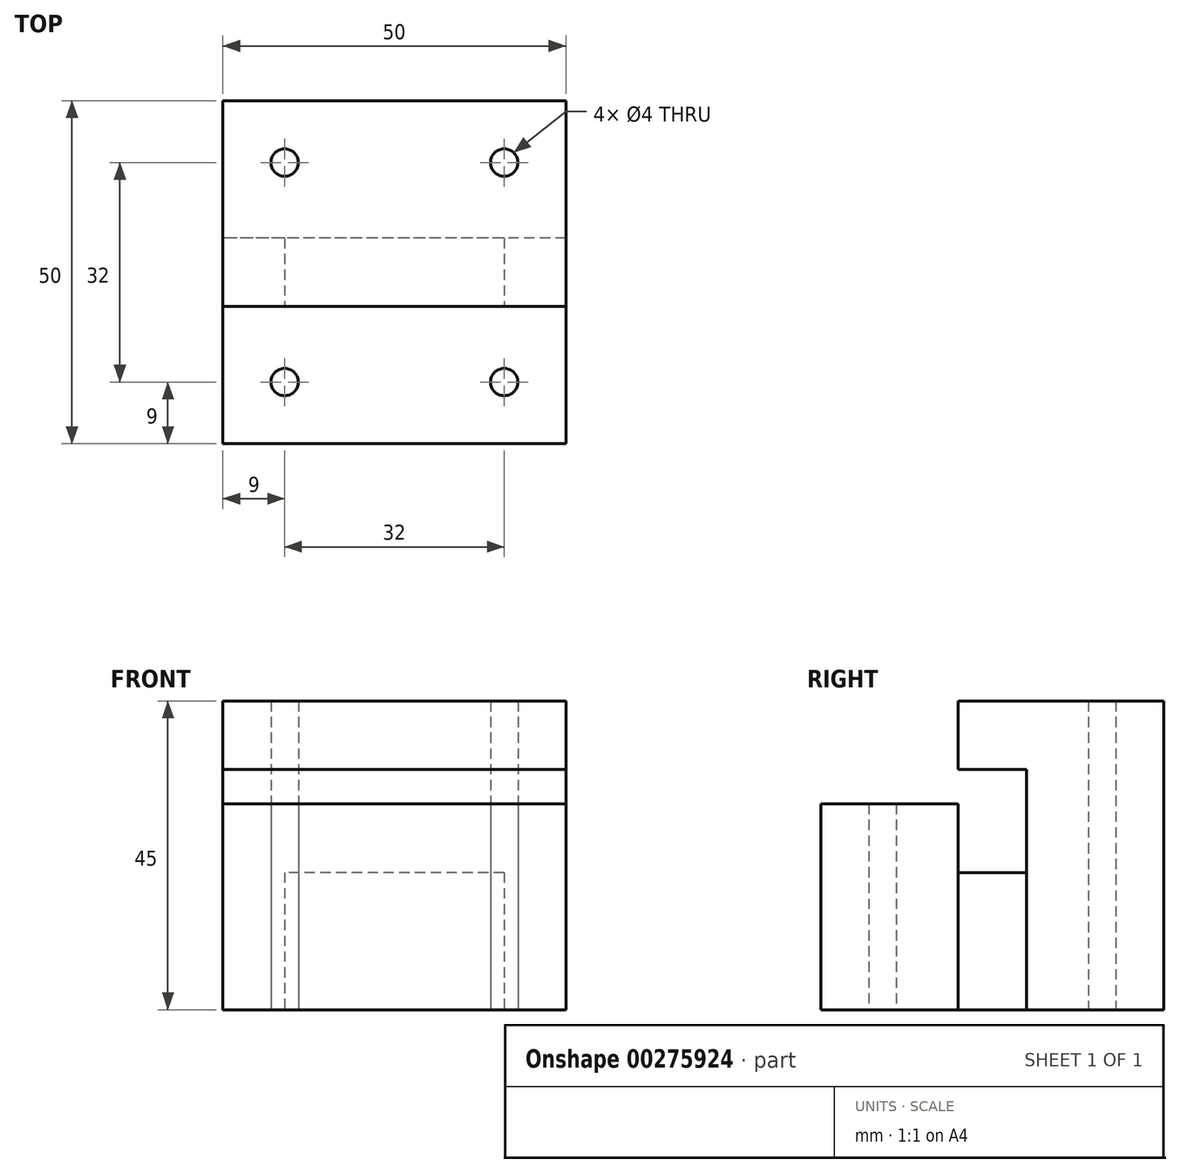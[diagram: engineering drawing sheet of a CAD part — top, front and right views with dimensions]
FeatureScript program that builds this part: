
annotation { "Feature Type Name" : "Feature", "Feature Type Description" : "" }
export const myFeature = defineFeature(function(context is Context, id is Id, definition is map)
    precondition{}
    {
        {
            var Q0;
            Q0=qCreatedBy(makeId("Top.planeOp"),FACE);
            var sketch = newSketch(context, id + "F0", { "sketchPlane" : qUnion([Q0])});
            skLineSegment(sketch, "E0.bottom", {"start": v(25, 25) * mm, "end": v(-25, 25) * mm});
            skLineSegment(sketch, "E0.top", {"start": v(25, -25) * mm, "end": v(-25, -25) * mm});
            skLineSegment(sketch, "E0.left", {"start": v(25, 25) * mm, "end": v(25, -25) * mm});
            skLineSegment(sketch, "E0.right", {"start": v(-25, 25) * mm, "end": v(-25, -25) * mm});
            skPoint(sketch, "E0.middle", {"position": v(0, 0) * mm});
            skLineSegment(sketch, "E1.bottom", {"start": v(16, 16) * mm, "end": v(-16, 16) * mm});
            skLineSegment(sketch, "E1.top", {"start": v(16, -16) * mm, "end": v(-16, -16) * mm});
            skLineSegment(sketch, "E1.left", {"start": v(16, 16) * mm, "end": v(16, -16) * mm});
            skLineSegment(sketch, "E1.right", {"start": v(-16, 16) * mm, "end": v(-16, -16) * mm});
            skPoint(sketch, "E2", {"position": v(-16, 16) * mm});
            skPoint(sketch, "E3", {"position": v(16, 16) * mm});
            skPoint(sketch, "E4", {"position": v(16, -16) * mm});
            skPoint(sketch, "E5", {"position": v(-16, -16) * mm});
            skLineSegment(sketch, "E6.bottom", {"start": v(25, 5) * mm, "end": v(-25, 5) * mm});
            skLineSegment(sketch, "E6.top", {"start": v(25, -5) * mm, "end": v(-25, -5) * mm});
            skLineSegment(sketch, "E6.left", {"start": v(25, 5) * mm, "end": v(25, -5) * mm});
            skLineSegment(sketch, "E6.right", {"start": v(-25, 5) * mm, "end": v(-25, -5) * mm});
            skSolve(sketch);
        }
        {
            var Q0;
            {var subQ2=sQuery(id+"F0.wireOp",EDGE,"E0.top");Q0=makeQuery(id+"F0.imprint","IMPRINT",FACE,{"disambiguationData":[TD([[makeQuery(id+"F0.imprint","IMPRINT",EDGE,{"derivedFrom":subQ2}),-1.0]])]});}
            var Q1;
            {var subQ0=sQuery(id+"F0.wireOp",EDGE,"E1.top");Q1=makeQuery(id+"F0.imprint","IMPRINT",FACE,{"disambiguationData":[TD([[makeQuery(id+"F0.imprint","IMPRINT",EDGE,{"derivedFrom":subQ0}),-1.0]])]});}
            extrude(context, id + "F1", {"entities" : qUnion([Q0, Q1]), "depth" : 30 * mm});
        }
        {
            var Q0;
            {var subQ5=sQuery(id+"F0.wireOp",EDGE,"E6.left");Q0=makeQuery(id+"F0.imprint","IMPRINT",FACE,{"disambiguationData":[TD([[makeQuery(id+"F0.imprint","IMPRINT",EDGE,{"derivedFrom":subQ5}),-1.0]])]});}
            var Q1;
            {var subQ0=sQuery(id+"F0.wireOp",EDGE,"E6.bottom");var subQ1=sQuery(id+"F0.wireOp",EDGE,"E1.left");var subQ2=makeQuery(id+"F0.imprint","INTERSECT",VERTEX,{"derivedFrom":[subQ1,subQ0]});Q1=makeQuery(id+"F0.imprint","IMPRINT",FACE,{"disambiguationData":[TD([[makeQuery(id+"F0.imprint","IMPRINT",EDGE,{"disambiguationData":[TD([[subQ2,-1.0]])],"derivedFrom":subQ1}),-1.0]])]});}
            var Q2;
            {var subQ5=sQuery(id+"F0.wireOp",EDGE,"E6.right");Q2=makeQuery(id+"F0.imprint","IMPRINT",FACE,{"disambiguationData":[TD([[makeQuery(id+"F0.imprint","IMPRINT",EDGE,{"derivedFrom":subQ5}),1.0]])]});}
            extrude(context, id + "F2", {"entities" : qUnion([Q0, Q1, Q2]), "depth" : 20 * mm});
        }
        {
            var Q0;
            Q0=sQuery(id+"F0.wireOp",VERTEX,"E2");
            var Q1;
            Q1=sQuery(id+"F0.wireOp",VERTEX,"E5");
            var Q2;
            Q2=sQuery(id+"F0.wireOp",VERTEX,"E3");
            var Q3;
            Q3=sQuery(id+"F0.wireOp",VERTEX,"E4");
            var Q4;
            Q4=makeQuery(id+"F1.opExtrude","SWEPT_BODY",BODY,{"disambiguationData":[OSD([sQuery(id+"F0.wireOp",EDGE,"E0.bottom"),sQuery(id+"F0.wireOp",EDGE,"E0.left"),sQuery(id+"F0.wireOp",EDGE,"E0.right"),sQuery(id+"F0.wireOp",EDGE,"E6.bottom")])]});
            var Q5;
            Q5=makeQuery(id+"F1.opExtrude","SWEPT_BODY",BODY,{"disambiguationData":[OSD([sQuery(id+"F0.wireOp",EDGE,"E0.top"),sQuery(id+"F0.wireOp",EDGE,"E0.left"),sQuery(id+"F0.wireOp",EDGE,"E0.right"),sQuery(id+"F0.wireOp",EDGE,"E6.top")])]});
            hole(context, id + "F3", {"style" : HoleStyle.SIMPLE, "endStyle" : HoleEndStyle.THROUGH, "oppositeDirection" : true, "holeDiameter" : 4 * mm, "tappedDepth" : 12 * mm, "tapClearance" : 3, "locations" : qUnion([Q0, Q1, Q2, Q3]), "scope" : qUnion([Q4, Q5])});
        }
        {
            var Q0;
            {var subQ2=sQuery(id+"F0.wireOp",EDGE,"E0.bottom");Q0=makeQuery(id+"F0.imprint","IMPRINT",FACE,{"disambiguationData":[TD([[makeQuery(id+"F0.imprint","IMPRINT",EDGE,{"derivedFrom":subQ2}),1.0]])]});}
            var Q1;
            {var subQ0=sQuery(id+"F0.wireOp",EDGE,"E1.bottom");Q1=makeQuery(id+"F0.imprint","IMPRINT",FACE,{"disambiguationData":[TD([[makeQuery(id+"F0.imprint","IMPRINT",EDGE,{"derivedFrom":subQ0}),1.0]])]});}
            extrude(context, id + "F4", {"entities" : qUnion([Q0, Q1]), "operationType" : NewBodyOperationType.ADD, "depth" : 45 * mm});
        }
        {
            var Q0;
            Q0=makeQuery(id+"F4.opExtrude","CAP_FACE",FACE,{"disambiguationData":[OSD([sQuery(id+"F0.wireOp",EDGE,"E0.bottom"),sQuery(id+"F0.wireOp",EDGE,"E0.left"),sQuery(id+"F0.wireOp",EDGE,"E0.right"),sQuery(id+"F0.wireOp",EDGE,"E6.bottom")])],"isStart":false});
            var sketch = newSketch(context, id + "F5", { "sketchPlane" : qUnion([Q0])});
            skLineSegment(sketch, "E7.bottom", {"start": v(-25, 5) * mm, "end": v(25, 5) * mm});
            skLineSegment(sketch, "E7.top", {"start": v(-25, -5) * mm, "end": v(25, -5) * mm});
            skLineSegment(sketch, "E7.left", {"start": v(-25, 5) * mm, "end": v(-25, -5) * mm});
            skLineSegment(sketch, "E7.right", {"start": v(25, 5) * mm, "end": v(25, -5) * mm});
            skSolve(sketch);
        }
        {
            var Q0;
            Q0 = qSketchRegion(id + "F5", true);
            extrude(context, id + "F6", {"entities" : qUnion([Q0]), "operationType" : NewBodyOperationType.ADD, "oppositeDirection" : true, "depth" : 10 * mm});
        }
        {
            var Q0;
            Q0=sQuery(id+"F0.wireOp",VERTEX,"E2");
            var Q1;
            Q1=sQuery(id+"F0.wireOp",VERTEX,"E3");
            var Q2;
            Q2=makeQuery(id+"F2.opExtrude","SWEPT_BODY",BODY,{"disambiguationData":[OSD([sQuery(id+"F0.wireOp",EDGE,"E6.bottom"),sQuery(id+"F0.wireOp",EDGE,"E6.top"),sQuery(id+"F0.wireOp",EDGE,"E6.left"),sQuery(id+"F0.wireOp",EDGE,"E6.right")])]});
            hole(context, id + "F7", {"style" : HoleStyle.SIMPLE, "endStyle" : HoleEndStyle.THROUGH, "oppositeDirection" : true, "holeDiameter" : 4 * mm, "tappedDepth" : 12 * mm, "tapClearance" : 3, "locations" : qUnion([Q0, Q1]), "scope" : qUnion([Q2])});
        }
    });
